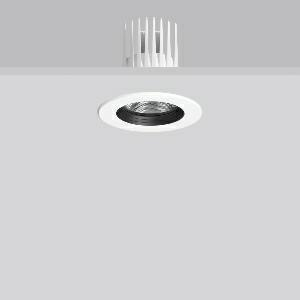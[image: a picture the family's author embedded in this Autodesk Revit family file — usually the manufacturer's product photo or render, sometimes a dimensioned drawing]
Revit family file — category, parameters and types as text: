
# Revit family: heledon_mini_e_901749_002_2_a8b4
name_source: partatom
category: Lighting Fixtures
units: mm (PartAtom-declared; Revit-internal decimal feet)

## family parameters
Cut with Voids When Loaded = No
Host = Face
Light Source = No
Part Type = Normal
Room Calculation Point = No
Round Connector Dimension = Use Diameter
Shared = No

## types (1)
- HELEDON mini E (1 x LED Modul 927, 3300 lm, 2700)
    Apparent Load = 29 VA
    Approval mark = CE
    CIE Flux Codes = 99 100 100 100 100
    Color Rendering = 92
    Color Temperature = 2700
    Default Elevation = 1800 mm
    Description = Series: HELEDON mini
Round recessed downlight. Housing: die-cast aluminium, powder-coated. Black plastic ring and recessed LED to prevent glare from the side. Optical assembly with reflector made of MIRO-Silver with 98% total light reflection for outstanding efficiency - can be changed without tools. Best colour rendering index Ra>90. Suitable for Recessed ceiling mounting. Installation without tools thanks to spring fastening system. Including separate LED converter with connecting cable 600 mm.High quality converter without flickering and stroboscopic effect. Through-wiring box (5 pole) available as accessory. The following accessories can be mounted without use of tools: interchangeable lenses, decorative glasses, honeycomb louvre, clear and frosted diffusers, white interchangeable plastic ring. 
Colour: traffic white, matt (RAL 9016)
Diameter: 124 mm
Height: 3 mm
Cut-out diameter: 114 mm
Recess height: 170 mm
Luminaire: recess height: 120 mm
Lamp: LED
Socket: without socket
Colour temperature: 2700K
Colour rendering index (CRI): 92
System power: 29 W
Rated luminous flux: 3300 lm
Luminous efficiency: 114 lm/W
Control gear: Regulated power supply
Protection class: II
Type of protection: IP 20
    Height = 0 mm  [stored 0 ft]
    Lamp = 1 x LED Modul 927
    Lamp Light Flux = 3300 lm
    Lamp count = 1
    Length = 124 mm  [stored 0.406824 ft]
    Lifetime = 50000 h
    Luminous efficacy = 114 lm/W
    Manufacturer = RZB
    ModVariant = No
    Model = 901749.002.2
    Mounting Place = Ceiling
    Mounting Type = Recessed
    Number of Poles = 1
    OnlyDefault = Yes
    Power Factor = 1
    Product Name = HELEDON mini E
    Product group = Recessed downlights
    ProductGroupID = 402
    Protection Class = Protection class II
    Protection Degree = IP 20
    RLX_Detail_Level = 1
    RLX_Emergency_Light_Flux = 0 lm
    RLX_Emergency_Type = 0
    RLX_Emergency_Type_DB = No
    RlxData = <blob elided: 130877 chars, md5=77003c5f>
    Socket = socket
    Standby Power = 0 W
    System Light Flux = 3300 lm
    System Power = 29 W
    Type Comments = Product without accessories
    Type Image = 901657.002.jpg
    URL = http://relux.com
    VarID = ---
    Voltage = 230 V
    Voltage Range = 220-240 V
    Weight = 0.00 kg
    Width = 0 mm  [stored 0 ft]

note: [stored X ft] marks values corroborated as IEEE doubles in the binary element streams (Revit-internal decimal feet)

## geometry (parser evidence)
native form markers: Blend x4, Sweep x11
no freeform markers — native parametric forms only
